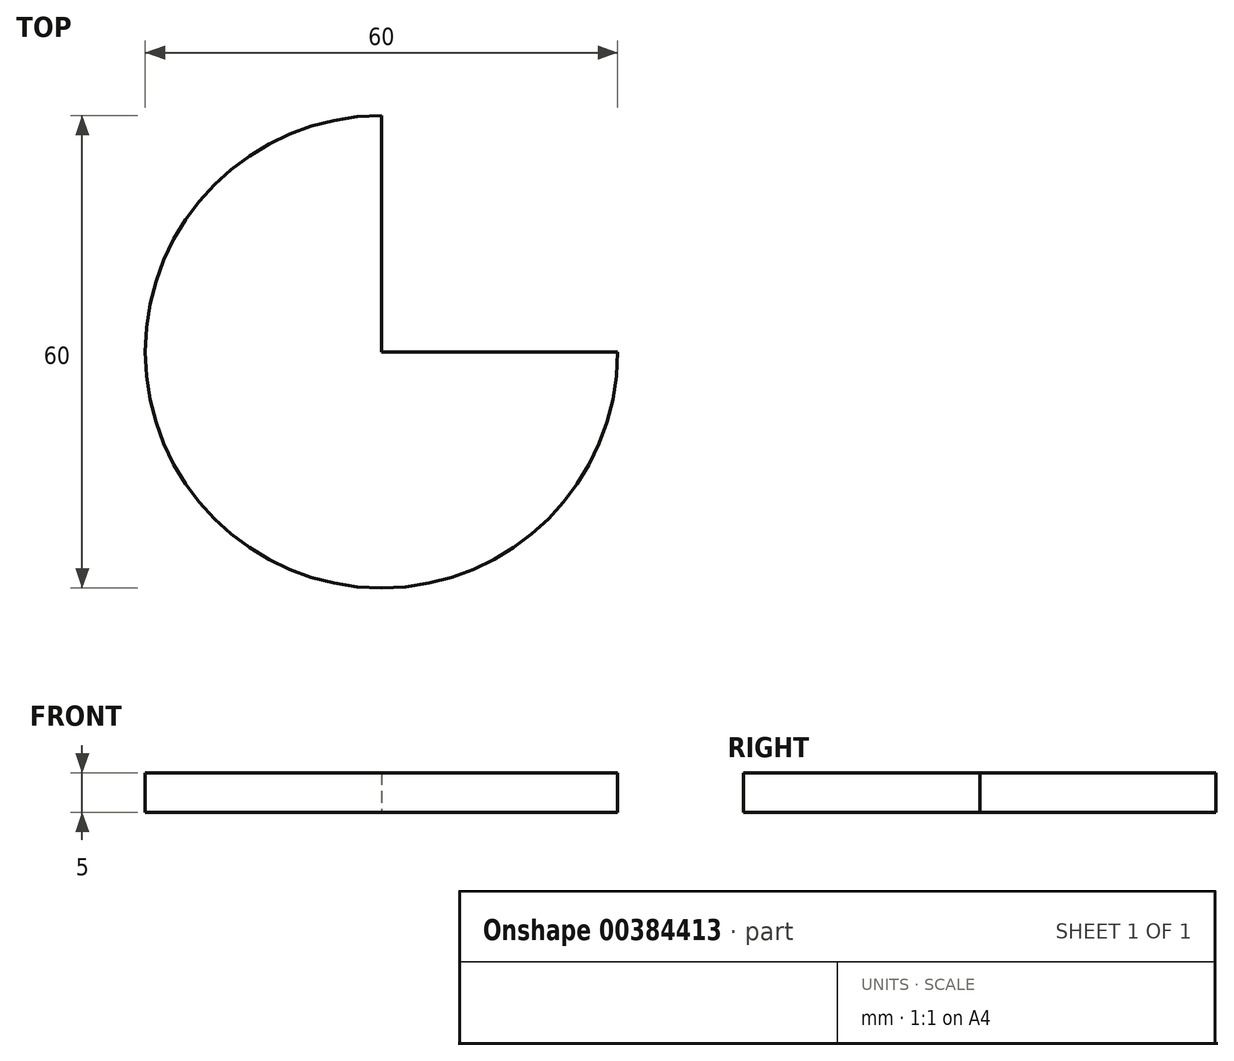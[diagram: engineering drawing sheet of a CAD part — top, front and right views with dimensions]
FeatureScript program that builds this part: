
annotation { "Feature Type Name" : "Feature", "Feature Type Description" : "" }
export const myFeature = defineFeature(function(context is Context, id is Id, definition is map)
    precondition{}
    {
        {
            var Q0;
            Q0=qCreatedBy(makeId("Top.planeOp"),FACE);
            var sketch = newSketch(context, id + "F0", { "sketchPlane" : qUnion([Q0])});
            skArc(sketch, "E0", {"start": v(0, 30) * mm, "mid": v(-21.21, -21.21) * mm, "end": v(30, 0) * mm});
            skLineSegment(sketch, "E1", {"start": v(0, 0) * mm, "end": v(0, 30) * mm});
            skLineSegment(sketch, "E2", {"start": v(0, 0) * mm, "end": v(30, 0) * mm});
            skSolve(sketch);
        }
        {
            var Q0;
            Q0=makeQuery(id+"F0.imprint","IMPRINT",FACE,{"disambiguationData":[TD([[makeQuery(id+"F0.imprint","IMPRINT",EDGE,{"derivedFrom":sQuery(id+"F0.wireOp",EDGE,"E0")}),1.0]])]});
            extrude(context, id + "F1", {"entities" : qUnion([Q0]), "depth" : 5 * mm});
        }
    });
